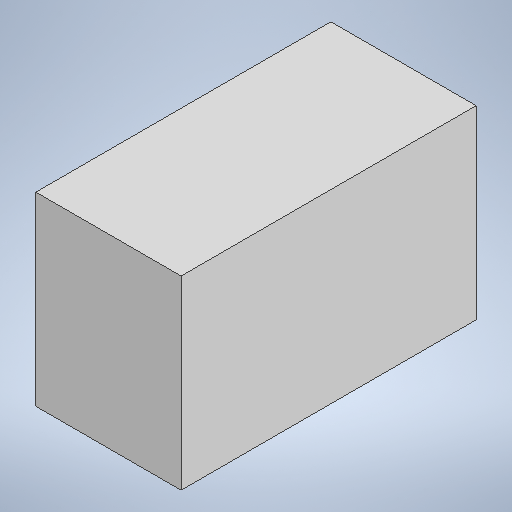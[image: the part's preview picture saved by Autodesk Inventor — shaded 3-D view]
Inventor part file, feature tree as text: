
AUTODESK INVENTOR PART (.ipt)
format: ipt  version: 2025.2 (Build 292293000, 293)  size: 180,736 bytes
history: native  units: mm
features: extrude x2, sketch x2
ambient origin geometry x8: Origin, YZ Plane, XZ Plane, XY Plane, X Axis, Y Axis, Z Axis, Center Point
bodies: Solid1 (feature_tree)
feature tree (4):
  extrude  "Extrusion1"  Depth=55.0mm
  extrude  "Extrusion5"  Depth=5.0mm
  sketch  "Sketch1"  dims[d0=122.0mm d1=55.0mm]
  sketch  "Sketch5"  dims[d2=78.0mm d3=0.0mm d10=5.0mm d11=5.0mm d20=65.0mm d21=132.0mm d22=5.0mm d23=0.0mm d24=0.5mm d25=0.872665mm d26=0.5mm d27=0.872665mm]
